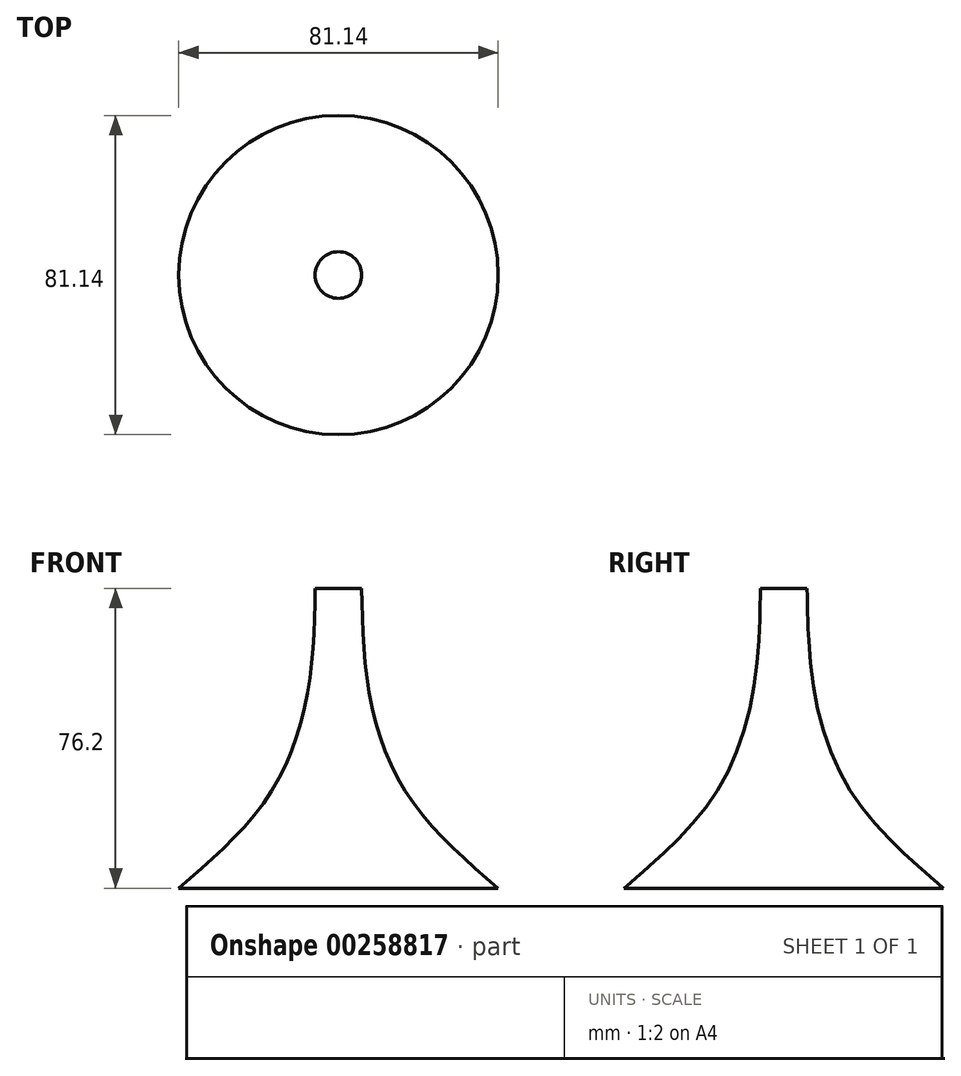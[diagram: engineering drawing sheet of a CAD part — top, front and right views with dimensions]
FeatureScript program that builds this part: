
annotation { "Feature Type Name" : "Feature", "Feature Type Description" : "" }
export const myFeature = defineFeature(function(context is Context, id is Id, definition is map)
    precondition{}
    {
        {
            var Q0;
            Q0=qCreatedBy(makeId("Top.planeOp"),FACE);
            var sketch = newSketch(context, id + "F0", { "sketchPlane" : qUnion([Q0])});
            skCircle(sketch, "E0", {"center": v(0, 0) * mm, "radius": 43.1 * mm});
            skCircle(sketch, "E1", {"center": v(0, 0) * mm, "radius": 40.57 * mm});
            skSolve(sketch);
        }
        {
            var Q0;
            Q0=qCreatedBy(makeId("Top.planeOp"),FACE);
            cPlane(context, id + "F1", {"entities" : qUnion([Q0]), "cplaneType" : CPlaneType.OFFSET, "offset" : 25.4 * mm, "width" : 152.4 * mm, "height" : 152.4 * mm});
        }
        {
            var Q0;
            Q0=qCreatedBy(id+"F1.planeOp",FACE);
            var sketch = newSketch(context, id + "F2", { "sketchPlane" : qUnion([Q0])});
            skCircle(sketch, "E2", {"center": v(0, 0) * mm, "radius": 19.05 * mm});
            skCircle(sketch, "E3", {"center": v(0, 0) * mm, "radius": 16.51 * mm});
            skSolve(sketch);
        }
        {
            var Q0;
            Q0=qCreatedBy(id+"F1.planeOp",FACE);
            cPlane(context, id + "F3", {"entities" : qUnion([Q0]), "cplaneType" : CPlaneType.OFFSET, "offset" : 25.4 * mm, "width" : 152.4 * mm, "height" : 152.4 * mm});
        }
        {
            var Q0;
            Q0=qCreatedBy(id+"F3.planeOp",FACE);
            var sketch = newSketch(context, id + "F4", { "sketchPlane" : qUnion([Q0])});
            skCircle(sketch, "E4", {"center": v(0, 0) * mm, "radius": 10.16 * mm});
            skCircle(sketch, "E5", {"center": v(0, 0) * mm, "radius": 7.62 * mm});
            skSolve(sketch);
        }
        {
            var Q0;
            Q0=qCreatedBy(id+"F3.planeOp",FACE);
            cPlane(context, id + "F5", {"entities" : qUnion([Q0]), "cplaneType" : CPlaneType.OFFSET, "offset" : 25.4 * mm, "width" : 152.4 * mm, "height" : 152.4 * mm});
        }
        {
            var Q0;
            Q0=qCreatedBy(id+"F5.planeOp",FACE);
            var sketch = newSketch(context, id + "F6", { "sketchPlane" : qUnion([Q0])});
            skCircle(sketch, "E6", {"center": v(0, 0) * mm, "radius": 8.46 * mm});
            skCircle(sketch, "E7", {"center": v(0, 0) * mm, "radius": 5.92 * mm});
            skSolve(sketch);
        }
        {
            var Q0;
            Q0=makeQuery(id+"F0.imprint","IMPRINT",FACE,{"disambiguationData":[TD([[makeQuery(id+"F0.imprint","IMPRINT",EDGE,{"derivedFrom":sQuery(id+"F0.wireOp",EDGE,"E1")}),1.0]])]});
            var Q1;
            Q1=makeQuery(id+"F2.imprint","IMPRINT",FACE,{"disambiguationData":[TD([[makeQuery(id+"F2.imprint","IMPRINT",EDGE,{"derivedFrom":sQuery(id+"F2.wireOp",EDGE,"E3")}),1.0]])]});
            var Q2;
            Q2=makeQuery(id+"F4.imprint","IMPRINT",FACE,{"disambiguationData":[TD([[makeQuery(id+"F4.imprint","IMPRINT",EDGE,{"derivedFrom":sQuery(id+"F4.wireOp",EDGE,"E5")}),1.0]])]});
            var Q3;
            Q3=makeQuery(id+"F6.imprint","IMPRINT",FACE,{"disambiguationData":[TD([[makeQuery(id+"F6.imprint","IMPRINT",EDGE,{"derivedFrom":sQuery(id+"F6.wireOp",EDGE,"E7")}),1.0]])]});
            loft(context, id + "F7", {"sheetProfilesArray" : [{ "sheetProfileEntities" : qUnion([Q0]) }, { "sheetProfileEntities" : qUnion([Q1]) }, { "sheetProfileEntities" : qUnion([Q2]) }, { "sheetProfileEntities" : qUnion([Q3]) }]});
        }
    });
